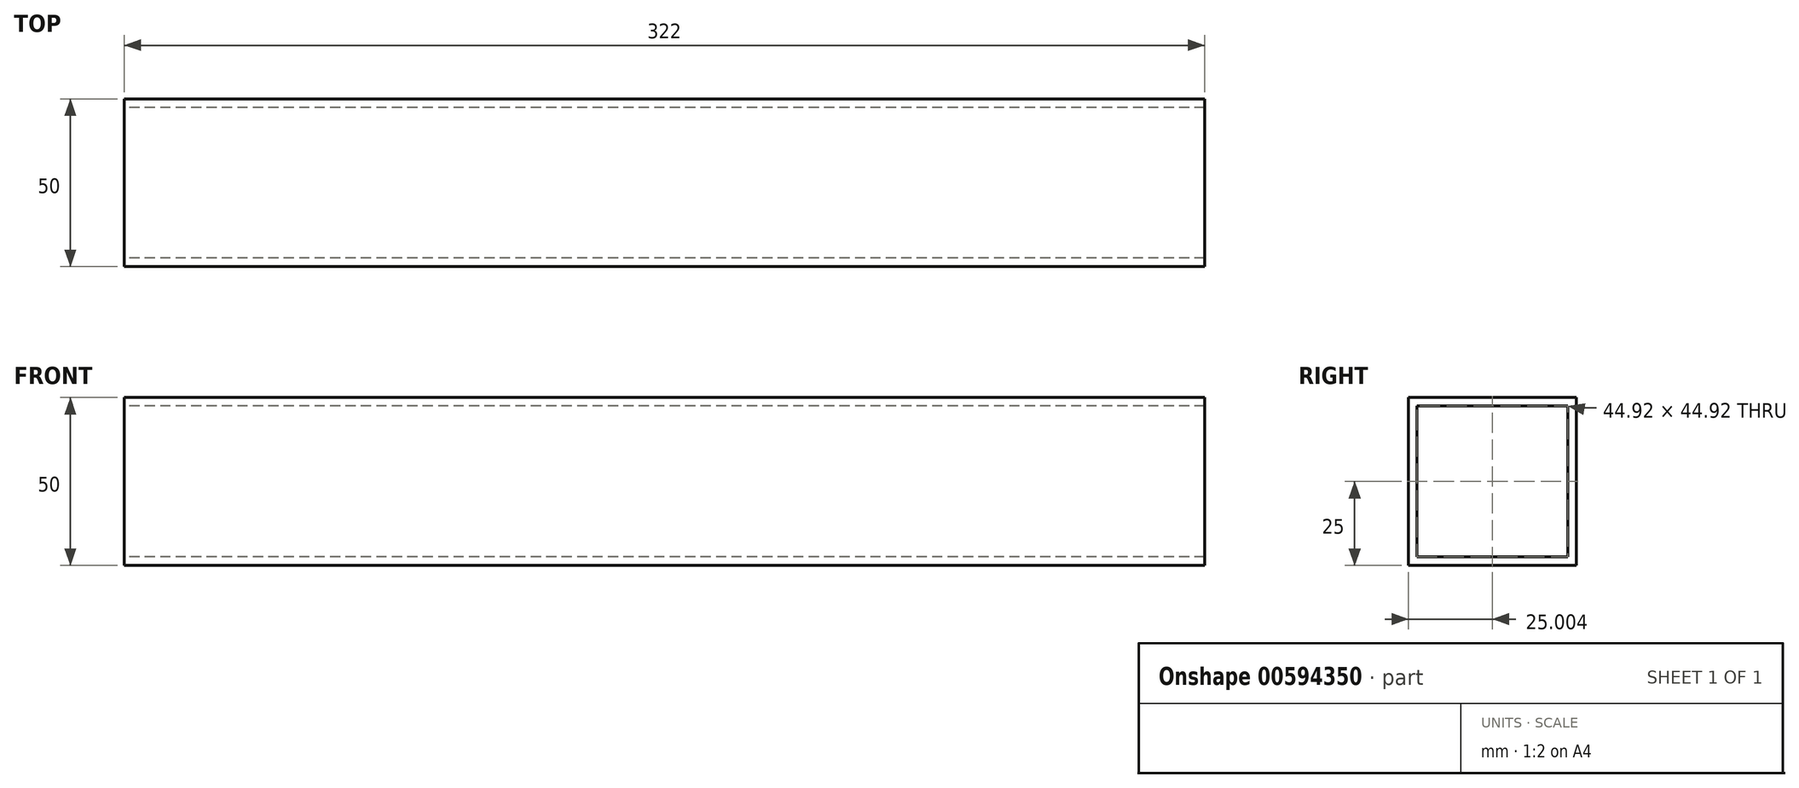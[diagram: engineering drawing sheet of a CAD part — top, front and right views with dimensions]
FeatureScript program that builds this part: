
annotation { "Feature Type Name" : "Feature", "Feature Type Description" : "" }
export const myFeature = defineFeature(function(context is Context, id is Id, definition is map)
    precondition{}
    {
        {
            var Q0;
            Q0=qCreatedBy(makeId("Top.planeOp"),FACE);
            var sketch = newSketch(context, id + "F0", { "sketchPlane" : qUnion([Q0])});
            skLineSegment(sketch, "E0.bottom", {"start": v(-53, -30.56) * mm, "end": v(-375, -30.56) * mm});
            skLineSegment(sketch, "E0.top", {"start": v(-53, 19.44) * mm, "end": v(-375, 19.44) * mm});
            skLineSegment(sketch, "E0.left", {"start": v(-53, -30.56) * mm, "end": v(-53, 19.44) * mm});
            skLineSegment(sketch, "E0.right", {"start": v(-375, -30.56) * mm, "end": v(-375, 19.44) * mm});
            skPoint(sketch, "E0.middle", {"position": v(-214, -5.56) * mm});
            skSolve(sketch);
        }
        {
            var Q0;
            Q0=makeQuery(id+"F0.imprint","IMPRINT",FACE,{"disambiguationData":[TD([[makeQuery(id+"F0.imprint","IMPRINT",EDGE,{"derivedFrom":sQuery(id+"F0.wireOp",EDGE,"E0.bottom")}),-1.0]])]});
            extrude(context, id + "F1", {"entities" : qUnion([Q0]), "depth" : 50 * mm, "offsetDistance" : 25.4 * mm});
        }
        {
            var Q0;
            Q0=makeQuery(id+"F1.opExtrude","SWEPT_FACE",FACE,{"disambiguationData":[OSD([sQuery(id+"F0.wireOp",EDGE,"E0.right")])]});
            var Q1;
            Q1=makeQuery(id+"F1.opExtrude","SWEPT_FACE",FACE,{"disambiguationData":[OSD([sQuery(id+"F0.wireOp",EDGE,"E0.left")])]});
            shell(context, id + "F2", {"entities" : qUnion([Q0, Q1]), "thickness" : 2.54 * mm});
        }
    });
